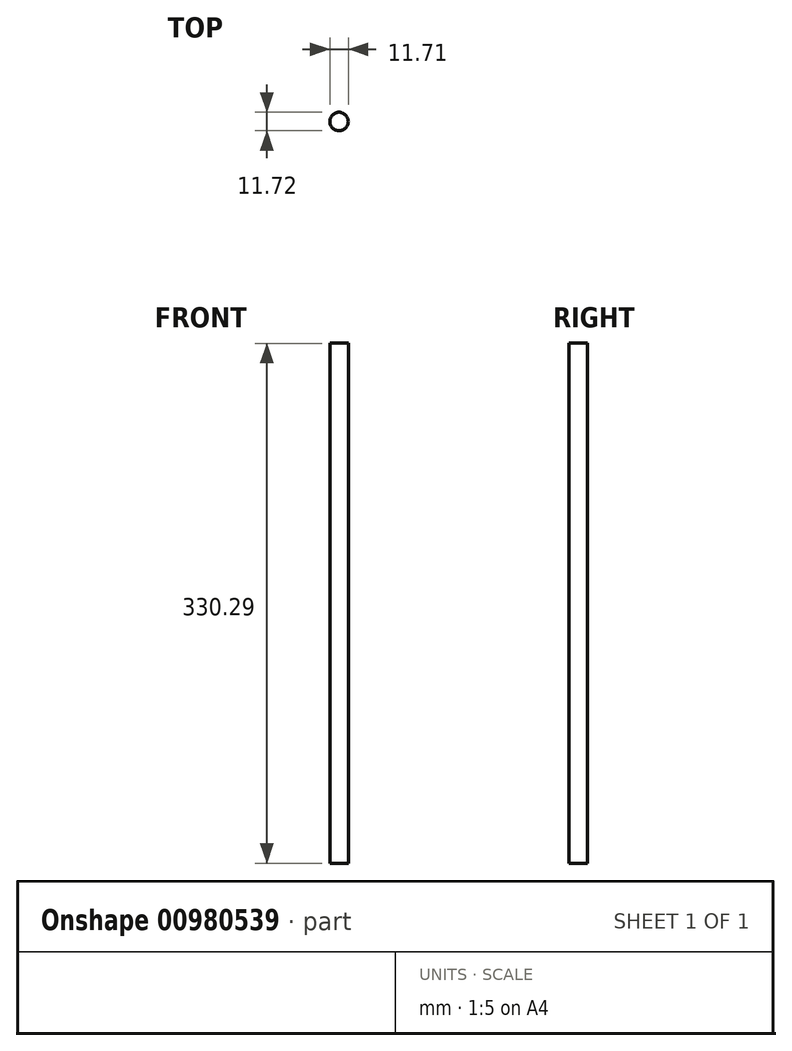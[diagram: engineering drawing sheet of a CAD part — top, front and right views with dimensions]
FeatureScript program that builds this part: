
annotation { "Feature Type Name" : "Feature", "Feature Type Description" : "" }
export const myFeature = defineFeature(function(context is Context, id is Id, definition is map)
    precondition{}
    {
        {
            var Q0;
            Q0=qCreatedBy(makeId("Front.planeOp"),FACE);
            var sketch = newSketch(context, id + "F0", { "sketchPlane" : qUnion([Q0])});
            skLineSegment(sketch, "E0", {"start": v(-75.1, 171.76) * mm, "end": v(-75.1, -158.53) * mm});
            skLineSegment(sketch, "E1", {"start": v(-75.1, -158.53) * mm, "end": v(-69.24, -158.53) * mm});
            skLineSegment(sketch, "E2", {"start": v(-69.24, 171.76) * mm, "end": v(-75.1, 171.76) * mm});
            skPoint(sketch, "E3.orphan", {"position": v(-51.66, 171.76) * mm});
            skLineSegment(sketch, "E4", {"start": v(-69.24, 171.76) * mm, "end": v(-69.24, -158.53) * mm});
            skPoint(sketch, "E5.orphan", {"position": v(-63.38, -158.53) * mm});
            skPoint(sketch, "E6.orphan", {"position": v(-63.38, 171.76) * mm});
            skSolve(sketch);
        }
        {
            var Q0;
            Q0=makeQuery(id+"F0.imprint","IMPRINT",FACE,{"disambiguationData":[TD([[makeQuery(id+"F0.imprint","IMPRINT",EDGE,{"derivedFrom":sQuery(id+"F0.wireOp",EDGE,"E0")}),1.0]])]});
            var Q1;
            Q1=sQuery(id+"F0.wireOp",EDGE,"E4");
            revolve(context, id + "F1", {"surfaceOperationType" : NewSurfaceOperationType.NEW, "entities" : qUnion([Q0]), "axis" : qUnion([Q1]), "revolveType" : RevolveType.FULL});
        }
    });
